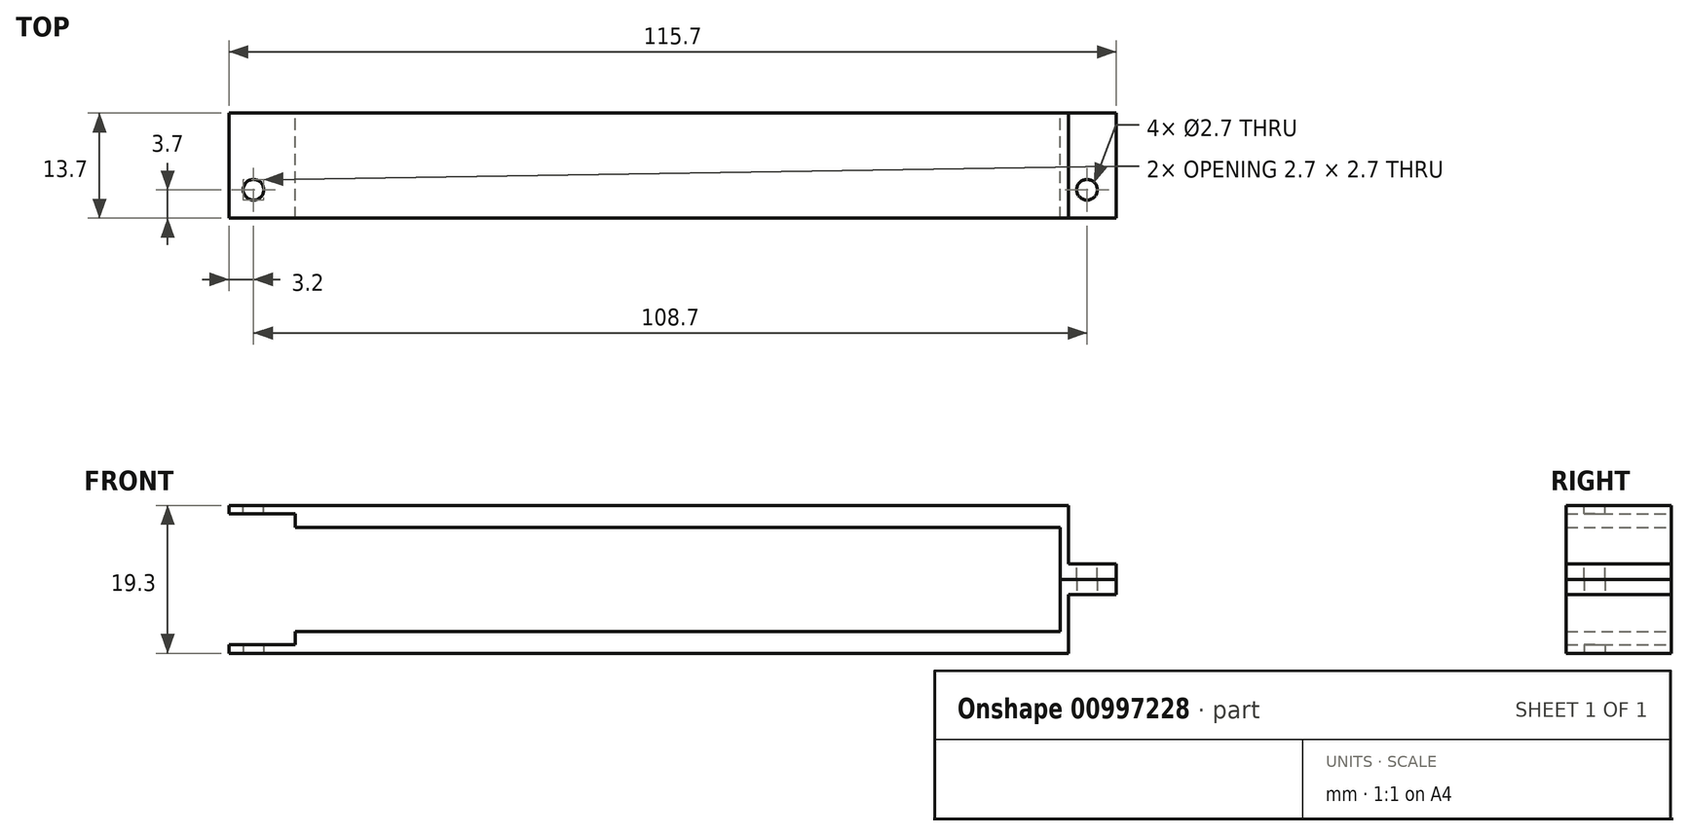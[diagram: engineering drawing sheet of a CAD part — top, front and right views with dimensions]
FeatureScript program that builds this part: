
annotation { "Feature Type Name" : "Feature", "Feature Type Description" : "" }
export const myFeature = defineFeature(function(context is Context, id is Id, definition is map)
    precondition{}
    {
        {
            var Q0;
            Q0=qCreatedBy(makeId("Front.planeOp"),FACE);
            var sketch = newSketch(context, id + "F0", { "sketchPlane" : qUnion([Q0])});
            skLineSegment(sketch, "E0", {"start": v(-61.78, 9.65) * mm, "end": v(47.72, 9.65) * mm});
            skLineSegment(sketch, "E1", {"start": v(47.72, 9.65) * mm, "end": v(47.72, 2) * mm});
            skLineSegment(sketch, "E2", {"start": v(47.72, 2) * mm, "end": v(53.92, 2) * mm});
            skLineSegment(sketch, "E3", {"start": v(53.92, 2) * mm, "end": v(53.92, 0) * mm});
            skLineSegment(sketch, "E4", {"start": v(53.92, 0) * mm, "end": v(46.62, 0) * mm});
            skLineSegment(sketch, "E5", {"start": v(46.62, 0) * mm, "end": v(46.62, 6.8) * mm});
            skLineSegment(sketch, "E6", {"start": v(46.62, 6.8) * mm, "end": v(-53.16, 6.8) * mm});
            skLineSegment(sketch, "E7", {"start": v(-53.16, 6.8) * mm, "end": v(-53.16, 8.55) * mm});
            skLineSegment(sketch, "E8", {"start": v(-53.16, 8.55) * mm, "end": v(-61.78, 8.55) * mm});
            skLineSegment(sketch, "E9", {"start": v(-61.78, 8.55) * mm, "end": v(-61.78, 9.65) * mm});
            skLineSegment(sketch, "E10", {"start": v(-58.58, -0.95) * mm, "end": v(-58.58, 26.62) * mm, "construction": true});
            skLineSegment(sketch, "E11", {"start": v(50.12, -12.65) * mm, "end": v(50.12, 32.83) * mm, "construction": true});
            skPoint(sketch, "E12", {"position": v(-58.58, 9.65) * mm});
            skPoint(sketch, "E13", {"position": v(50.12, 2) * mm});
            skSolve(sketch);
        }
        {
            var Q0;
            Q0 = qSketchRegion(id + "F0", true);
            extrude(context, id + "F1", {"entities" : qUnion([Q0]), "depth" : 3.7 * mm, "offsetDistance" : 25 * mm, "hasSecondDirection" : true, "secondDirectionOppositeDirection" : true, "secondDirectionDepth" : 10 * mm});
        }
        {
            var Q0;
            Q0=makeQuery(id+"F1.opExtrude","SWEPT_FACE",FACE,{"disambiguationData":[OSD([sQuery(id+"F0.wireOp",EDGE,"E0")])]});
            var sketch = newSketch(context, id + "F2", { "sketchPlane" : qUnion([Q0])});
            skPoint(sketch, "E14", {"position": v(-58.58, 0) * mm});
            skSolve(sketch);
        }
        {
            var Q0;
            Q0=makeQuery(id+"F1.opExtrude","SWEPT_FACE",FACE,{"disambiguationData":[OSD([sQuery(id+"F0.wireOp",EDGE,"E2")])]});
            var sketch = newSketch(context, id + "F3", { "sketchPlane" : qUnion([Q0])});
            skPoint(sketch, "E15", {"position": v(50.12, 0) * mm});
            skSolve(sketch);
        }
        {
            var Q0;
            Q0=sQuery(id+"F3.wireOp",VERTEX,"E15");
            var Q1;
            Q1=sQuery(id+"F2.wireOp",VERTEX,"E14");
            var Q2;
            Q2=makeQuery(id+"F1.opExtrude","SWEPT_BODY",BODY,{"disambiguationData":[OSD([sQuery(id+"F0.wireOp",EDGE,"E0"),sQuery(id+"F0.wireOp",EDGE,"E1"),sQuery(id+"F0.wireOp",EDGE,"E2"),sQuery(id+"F0.wireOp",EDGE,"E3"),sQuery(id+"F0.wireOp",EDGE,"E4"),sQuery(id+"F0.wireOp",EDGE,"E5"),sQuery(id+"F0.wireOp",EDGE,"E6"),sQuery(id+"F0.wireOp",EDGE,"E7"),sQuery(id+"F0.wireOp",EDGE,"E8"),sQuery(id+"F0.wireOp",EDGE,"E9")])]});
            hole(context, id + "F4", {"style" : HoleStyle.SIMPLE, "endStyle" : HoleEndStyle.THROUGH, "holeDiameter" : 2.7 * mm, "majorDiameter" : 5 * mm, "isTappedThrough" : true, "tappedDepth" : 12 * mm, "tapClearance" : 3, "locations" : qUnion([Q0, Q1]), "scope" : qUnion([Q2])});
        }
        {
            var Q0;
            Q0=makeQuery(id+"F1.opExtrude","SWEPT_BODY",BODY,{"disambiguationData":[OSD([sQuery(id+"F0.wireOp",EDGE,"E0"),sQuery(id+"F0.wireOp",EDGE,"E1"),sQuery(id+"F0.wireOp",EDGE,"E2"),sQuery(id+"F0.wireOp",EDGE,"E3"),sQuery(id+"F0.wireOp",EDGE,"E4"),sQuery(id+"F0.wireOp",EDGE,"E5"),sQuery(id+"F0.wireOp",EDGE,"E6"),sQuery(id+"F0.wireOp",EDGE,"E7"),sQuery(id+"F0.wireOp",EDGE,"E8"),sQuery(id+"F0.wireOp",EDGE,"E9")])]});
            var Q1;
            Q1=qCreatedBy(makeId("Top.planeOp"),FACE);
            mirror(context, id + "F5", {"entities" : qUnion([Q0]), "mirrorPlane" : qUnion([Q1])});
        }
    });
